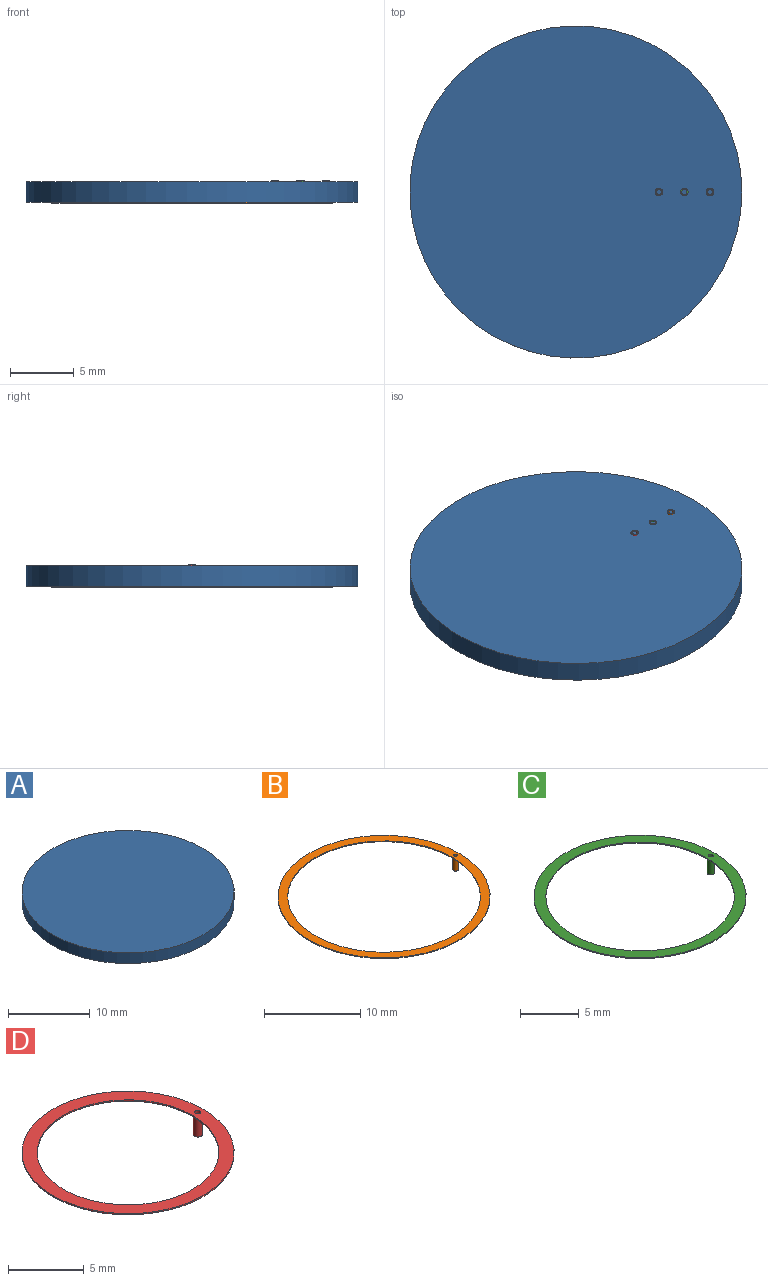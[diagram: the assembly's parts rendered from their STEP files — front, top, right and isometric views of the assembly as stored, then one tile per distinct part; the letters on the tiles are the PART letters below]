
ASSEMBLY  parts=4 mates=3
PART A: 3 faces, bbox 26x26x1.6 mm
  f0: cylinder r=13mm len=26mm, axis (0,0,1), area 130.7mm2, adj f1,f2
  f1: plane 26x26mm, normal (0,0,-1), area 530.9mm2, adj f0
  f2: plane 26x26mm, normal (0,0,1), area 530.9mm2, adj f0
PART B: 7 faces, bbox 22x22x1.8 mm
  f0: cylinder r=10mm len=20mm, axis (0,0,-1), area 6.3mm2, adj f2,f3
  f1: cylinder r=11mm len=22mm, axis (0,0,-1), area 6.9mm2, adj f2,f3
  f2: plane 22x22mm, normal (0,0,1), area 65.8mm2, adj f0,f1,f6
  f3: plane 22x22mm, normal (0,0,-1), area 65.7mm2, adj f0,f1,f4
  f4: cylinder r=0.3mm len=1.7mm, axis (0,0,1), area 3.2mm2, adj f3,f5
  f5: plane 0.6x0.6mm, normal (0,0,-1), area 0.2mm2, adj f4,f6
  f6: cylinder r=0.2mm len=1.8mm, axis (0,0,1), area 2.3mm2, adj f2,f5
PART C: 7 faces, bbox 18x18x1.8 mm
  f0: cylinder r=8mm len=16mm, axis (0,0,-1), area 5mm2, adj f2,f3
  f1: cylinder r=9mm len=18mm, axis (0,0,-1), area 5.7mm2, adj f2,f3
  f2: plane 18x18mm, normal (0,0,1), area 53.3mm2, adj f0,f1,f6
  f3: plane 18x18mm, normal (0,0,-1), area 53.1mm2, adj f0,f1,f4
  f4: cylinder r=0.3mm len=1.7mm, axis (0,0,1), area 3.2mm2, adj f3,f5
  f5: plane 0.6x0.6mm, normal (0,0,-1), area 0.2mm2, adj f4,f6
  f6: cylinder r=0.2mm len=1.8mm, axis (0,0,1), area 2.3mm2, adj f2,f5
PART D: 7 faces, bbox 14x14x1.8 mm
  f0: cylinder r=6mm len=12mm, axis (0,0,-1), area 3.8mm2, adj f2,f3
  f1: cylinder r=7mm len=14mm, axis (0,0,-1), area 4.4mm2, adj f2,f3
  f2: plane 14x14mm, normal (0,0,1), area 40.7mm2, adj f0,f1,f6
  f3: plane 14x14mm, normal (0,0,-1), area 40.6mm2, adj f0,f1,f4
  f4: cylinder r=0.3mm len=1.7mm, axis (0,0,1), area 3.2mm2, adj f3,f5
  f5: plane 0.6x0.6mm, normal (0,0,-1), area 0.2mm2, adj f4,f6
  f6: cylinder r=0.2mm len=1.8mm, axis (0,0,1), area 2.3mm2, adj f2,f5
PLACE A t=(0,0,1.6)mm
PLACE B rot(axis=(1,0,0),180deg) t=(0,0,0)mm
PLACE C rot(axis=(1,0,0),180deg) t=(0,0,0)mm
PLACE D rot(axis=(1,0,0),180deg) t=(0,0,0)mm
MATE fastened A.f0 <-> C.f0  axis (0,0,-1) through (0,0,0)mm
MATE fastened A.f0 <-> B.f0  axis (0,0,-1) through (0,0,0)mm
MATE fastened A.f0 <-> D.f0  axis (0,0,-1) through (0,0,0)mm
